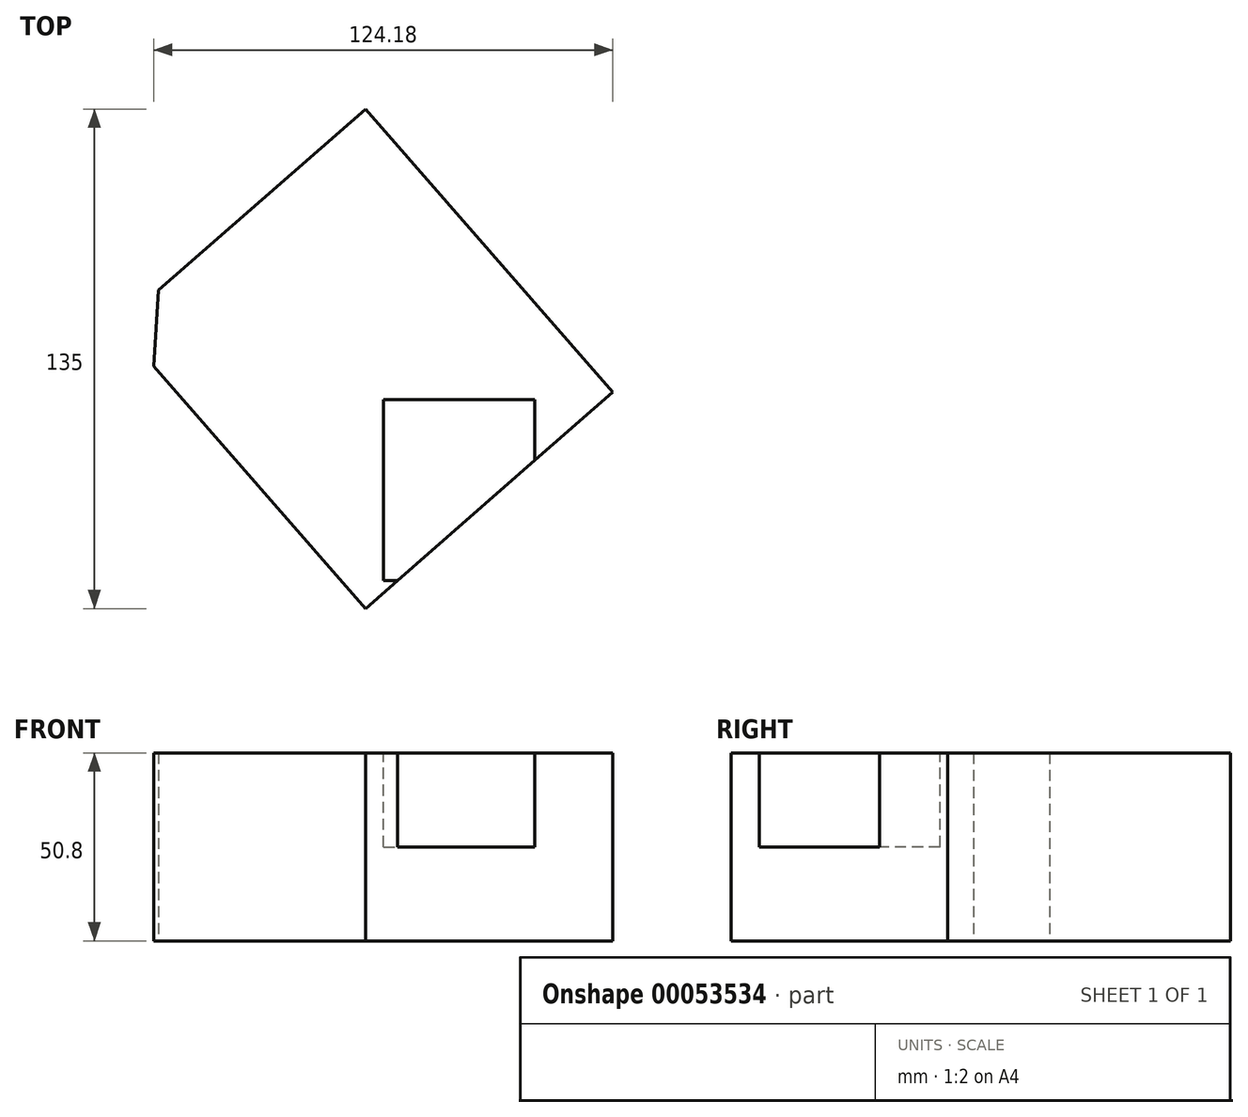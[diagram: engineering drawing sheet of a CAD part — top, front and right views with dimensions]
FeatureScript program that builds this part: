
annotation { "Feature Type Name" : "Feature", "Feature Type Description" : "" }
export const myFeature = defineFeature(function(context is Context, id is Id, definition is map)
    precondition{}
    {
        {
            var Q0;
            Q0=qCreatedBy(makeId("Top.planeOp"),FACE);
            var sketch = newSketch(context, id + "F0", { "sketchPlane" : qUnion([Q0])});
            skLineSegment(sketch, "E0", {"start": v(-55.9, 18.59) * mm, "end": v(0, 67.5) * mm});
            skLineSegment(sketch, "E1", {"start": v(0, 67.5) * mm, "end": v(66.9, -8.96) * mm});
            skLineSegment(sketch, "E2", {"start": v(66.9, -8.96) * mm, "end": v(0, -67.5) * mm});
            skLineSegment(sketch, "E3", {"start": v(0, -67.5) * mm, "end": v(-57.28, -2.04) * mm});
            skLineSegment(sketch, "E4", {"start": v(-57.28, -2.04) * mm, "end": v(-55.9, 18.59) * mm});
            skLineSegment(sketch, "E5", {"start": v(0, -67.5) * mm, "end": v(0, 67.5) * mm, "construction": true});
            skLineSegment(sketch, "E6", {"start": v(0, 0) * mm, "end": v(31.57, 0) * mm, "construction": true});
            skSolve(sketch);
        }
        {
            var Q0;
            Q0 = qSketchRegion(id + "F0", true);
            extrude(context, id + "F1", {"entities" : qUnion([Q0]), "depth" : 50.8 * mm});
        }
        {
            var Q0;
            Q0=makeQuery(id+"F1.opExtrude","CAP_FACE",FACE,{"disambiguationData":[OSD([sQuery(id+"F0.wireOp",EDGE,"E0"),sQuery(id+"F0.wireOp",EDGE,"E1"),sQuery(id+"F0.wireOp",EDGE,"E2"),sQuery(id+"F0.wireOp",EDGE,"E3"),sQuery(id+"F0.wireOp",EDGE,"E4")])],"isStart":false});
            var sketch = newSketch(context, id + "F2", { "sketchPlane" : qUnion([Q0])});
            skLineSegment(sketch, "E7.bottom", {"start": v(4.88, -11.06) * mm, "end": v(45.8, -11.06) * mm});
            skLineSegment(sketch, "E7.top", {"start": v(4.88, -59.92) * mm, "end": v(45.8, -59.92) * mm});
            skLineSegment(sketch, "E7.left", {"start": v(4.88, -11.06) * mm, "end": v(4.88, -59.92) * mm});
            skLineSegment(sketch, "E7.right", {"start": v(45.8, -11.06) * mm, "end": v(45.8, -59.92) * mm});
            skSolve(sketch);
        }
        {
            var Q0;
            Q0 = qSketchRegion(id + "F2", true);
            extrude(context, id + "F3", {"entities" : qUnion([Q0]), "operationType" : NewBodyOperationType.REMOVE, "oppositeDirection" : true, "depth" : 25.4 * mm});
        }
    });
